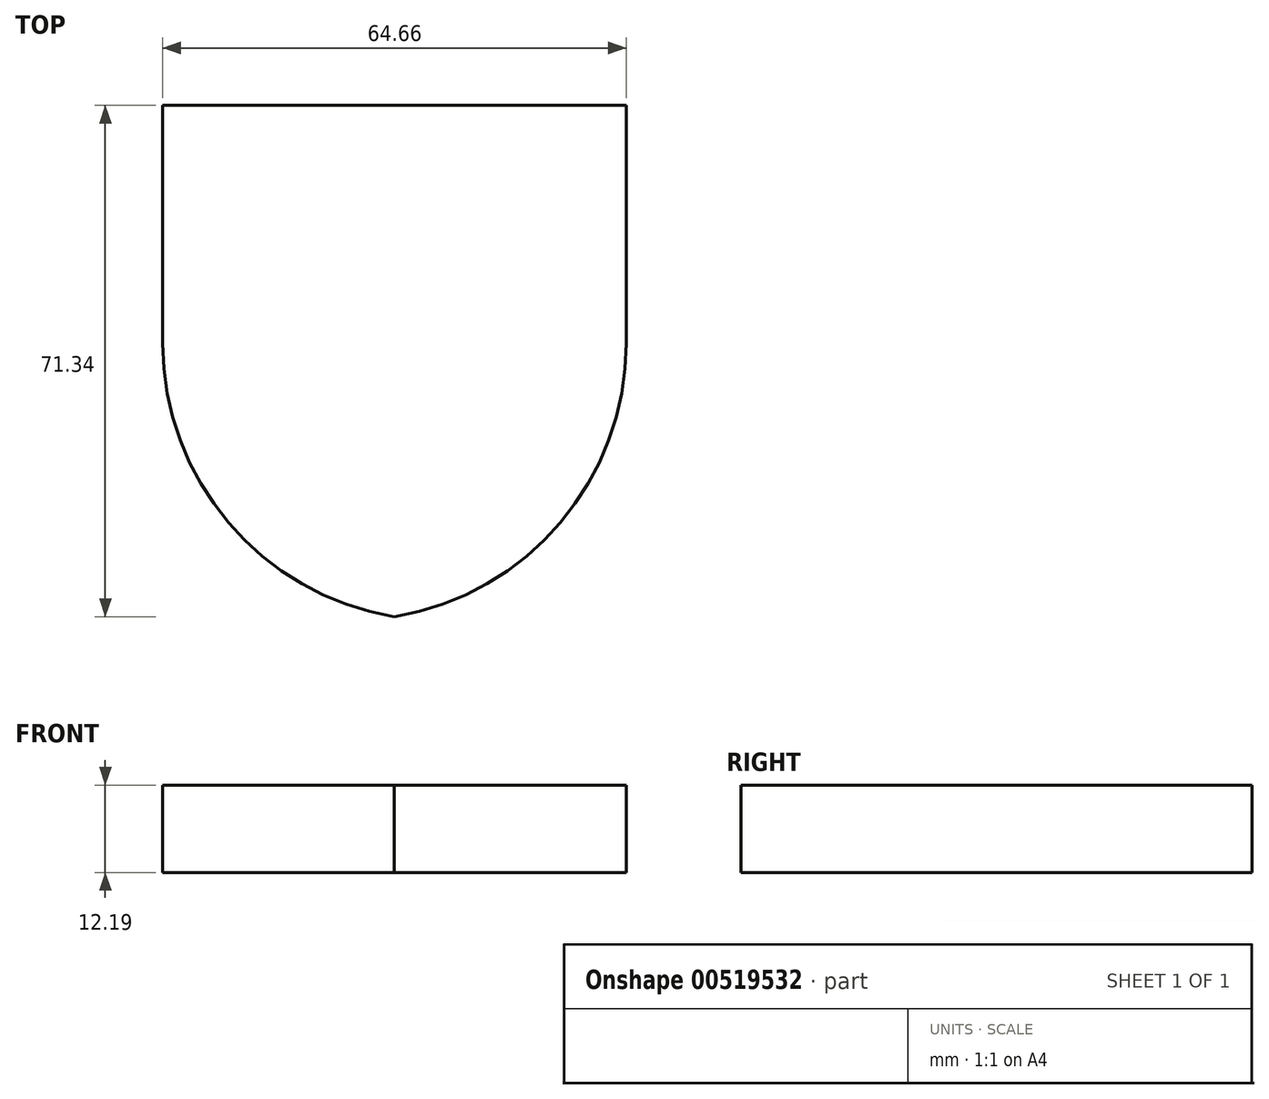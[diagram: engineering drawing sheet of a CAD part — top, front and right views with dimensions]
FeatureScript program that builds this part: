
annotation { "Feature Type Name" : "Feature", "Feature Type Description" : "" }
export const myFeature = defineFeature(function(context is Context, id is Id, definition is map)
    precondition{}
    {
        {
            var Q0;
            Q0=qCreatedBy(makeId("Top.planeOp"),FACE);
            var sketch = newSketch(context, id + "F0", { "sketchPlane" : qUnion([Q0])});
            skLineSegment(sketch, "E0.bottom", {"start": v(-25.03, 43.42) * mm, "end": v(39.63, 43.42) * mm});
            skLineSegment(sketch, "E0.top", {"start": v(-25.03, -28.44) * mm, "end": v(39.63, -28.44) * mm});
            skLineSegment(sketch, "E0.left", {"start": v(-25.03, 43.42) * mm, "end": v(-25.03, -28.44) * mm});
            skLineSegment(sketch, "E0.right", {"start": v(39.63, 43.42) * mm, "end": v(39.63, -28.44) * mm});
            skSolve(sketch);
        }
        {
            var Q0;
            Q0 = qSketchRegion(id + "F0", true);
            extrude(context, id + "F1", {"entities" : qUnion([Q0]), "depth" : 12.2 * mm, "offsetDistance" : 25.4 * mm});
        }
        {
            var Q0;
            Q0=makeQuery(id+"F1.opExtrude","SWEPT_EDGE",EDGE,{"disambiguationData":[OSD([sQuery(id+"F0.wireOp",EDGE,"E0.top"),sQuery(id+"F0.wireOp",EDGE,"E0.right")])]});
            var Q1;
            Q1=makeQuery(id+"F1.opExtrude","SWEPT_EDGE",EDGE,{"disambiguationData":[OSD([sQuery(id+"F0.wireOp",EDGE,"E0.top"),sQuery(id+"F0.wireOp",EDGE,"E0.left")])]});
            fillet(context, id + "F2", {"entities" : qUnion([Q0, Q1]), "radius" : 38.63 * mm, "tangentPropagation" : true, "allowEdgeOverflow" : false});
        }
    });
